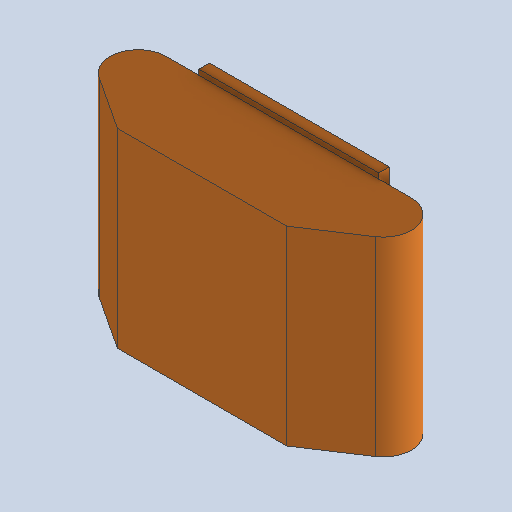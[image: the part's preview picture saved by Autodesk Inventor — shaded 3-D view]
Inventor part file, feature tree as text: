
AUTODESK INVENTOR PART (.ipt)
format: ipt  version: 2025 (Build 290162010, 162A)  size: 183,296 bytes
history: native  units: mm
features: extrude x3, sketch x3
ambient origin geometry x8: Origin, YZ Plane, XZ Plane, XY Plane, X Axis, Y Axis, Z Axis, Center Point
bodies: Solid1 (feature_tree)
feature tree (6):
  extrude  "Extrusion1"  Depth=102.0mm
  extrude  "Extrusion2"  Depth=80.0mm
  extrude  "Extrusion3"  Depth=180.0mm TaperAngle=0.0deg
  sketch  "Sketch1"  dims[d7=285.0mm d8=102.0mm]
  sketch  "Sketch2"  dims[d9=82.0mm d13=80.0mm]
  sketch  "Sketch3"  dims[d14=80.0mm d15=180.0mm d16=0.0mm d17=190.0mm d18=170.0mm d19=10.0mm d20=0.0mm d21=138.0mm d22=102.0mm d23=0.0mm d24=0.5mm d25=0.872665mm]
